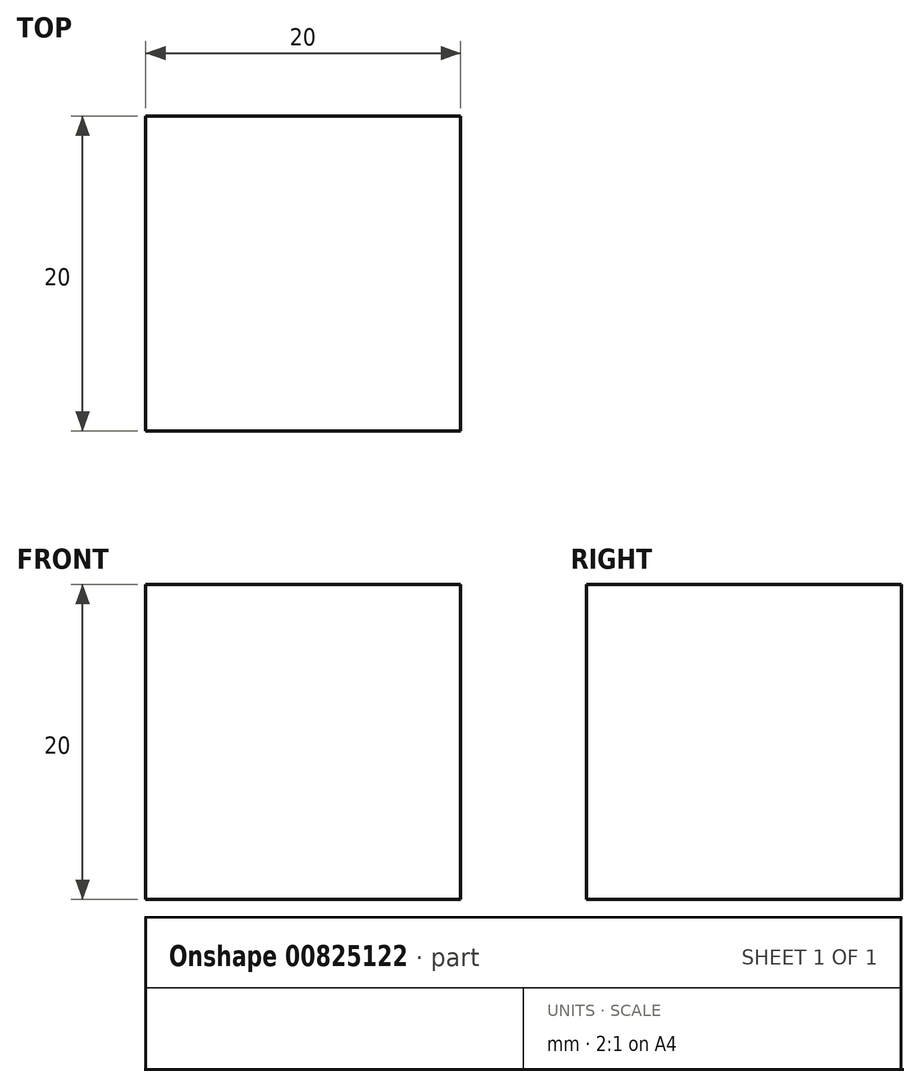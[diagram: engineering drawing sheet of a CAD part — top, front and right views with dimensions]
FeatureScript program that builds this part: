
annotation { "Feature Type Name" : "Feature", "Feature Type Description" : "" }
export const myFeature = defineFeature(function(context is Context, id is Id, definition is map)
    precondition{}
    {
        {
            var Q0;
            Q0=qCreatedBy(makeId("Top.planeOp"),FACE);
            var sketch = newSketch(context, id + "F0", { "sketchPlane" : qUnion([Q0])});
            skLineSegment(sketch, "E0.bottom", {"start": v(-9.51, 13.97) * mm, "end": v(10.49, 13.97) * mm});
            skLineSegment(sketch, "E0.top", {"start": v(-9.51, -6.03) * mm, "end": v(10.49, -6.03) * mm});
            skLineSegment(sketch, "E0.left", {"start": v(-9.51, 13.97) * mm, "end": v(-9.51, -6.03) * mm});
            skLineSegment(sketch, "E0.right", {"start": v(10.49, 13.97) * mm, "end": v(10.49, -6.03) * mm});
            skSolve(sketch);
        }
        {
            var Q0;
            Q0 = qSketchRegion(id + "F0", true);
            extrude(context, id + "F1", {"entities" : qUnion([Q0]), "depth" : 20 * mm, "offsetDistance" : 25 * mm});
        }
    });
